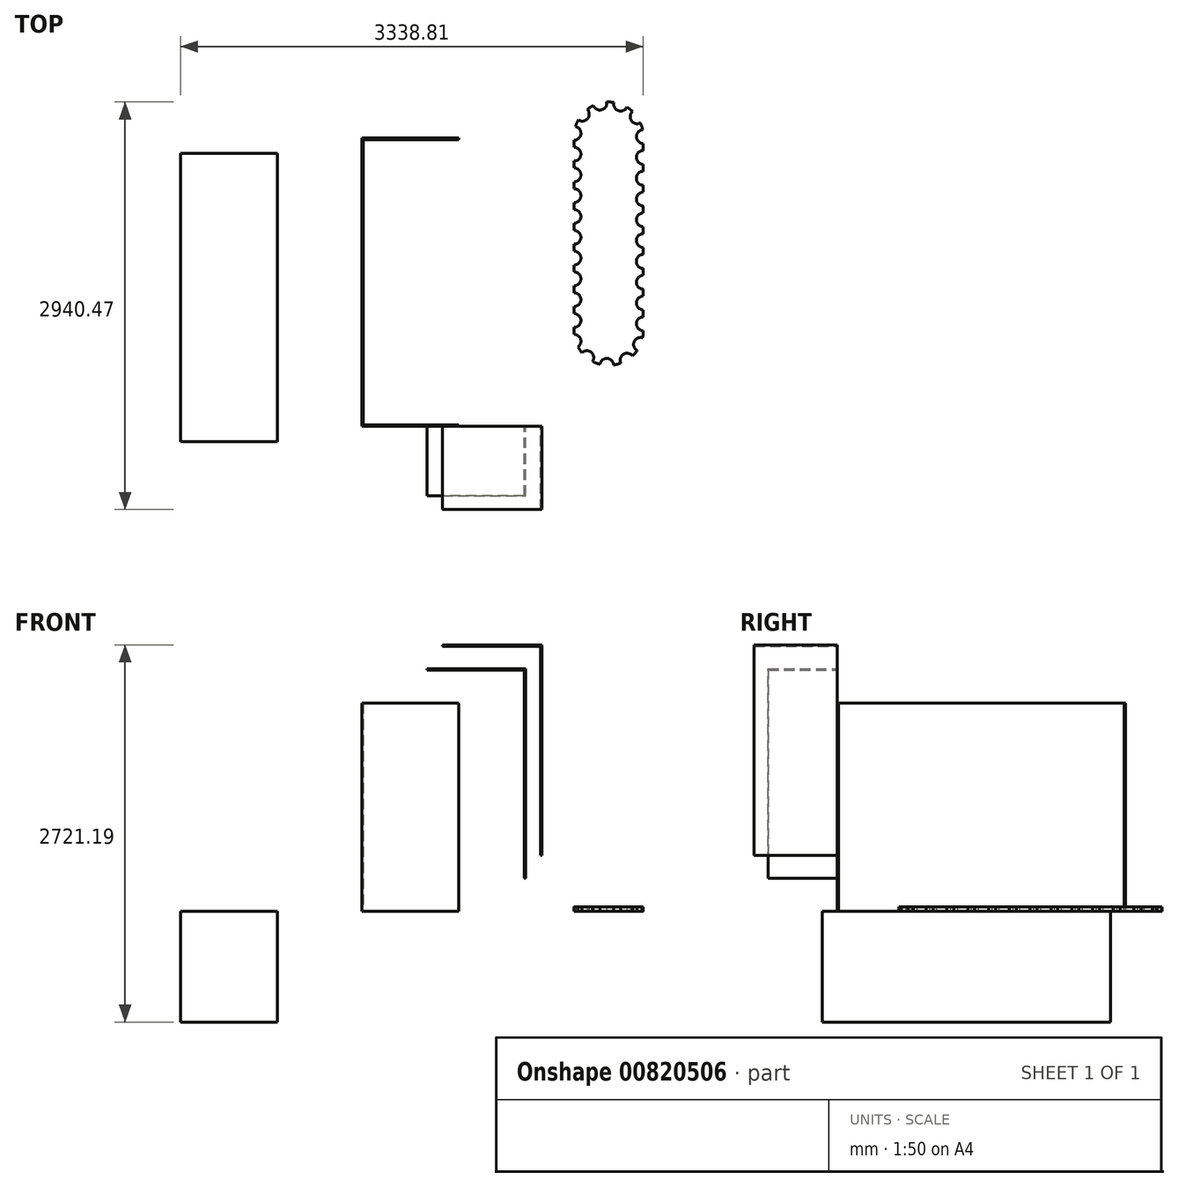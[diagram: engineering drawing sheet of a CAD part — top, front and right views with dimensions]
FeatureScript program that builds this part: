
annotation { "Feature Type Name" : "Feature", "Feature Type Description" : "" }
export const myFeature = defineFeature(function(context is Context, id is Id, definition is map)
    precondition{}
    {
        {
            var Q0;
            Q0=qCreatedBy(makeId("Top.planeOp"),FACE);
            var sketch = newSketch(context, id + "F0", { "sketchPlane" : qUnion([Q0])});
            skLineSegment(sketch, "E0", {"start": v(535.64, 2031.82) * mm, "end": v(535.64, -48.18) * mm});
            skLineSegment(sketch, "E1", {"start": v(535.64, -48.18) * mm, "end": v(-164.36, -48.18) * mm});
            skLineSegment(sketch, "E2", {"start": v(-164.36, -48.18) * mm, "end": v(-164.36, 2031.82) * mm});
            skLineSegment(sketch, "E3", {"start": v(-164.36, 2031.82) * mm, "end": v(535.64, 2031.82) * mm});
            skSolve(sketch);
        }
        {
            var Q0;
            Q0=makeQuery(id+"F0.imprint","IMPRINT",FACE,{"disambiguationData":[TD([[makeQuery(id+"F0.imprint","IMPRINT",EDGE,{"derivedFrom":sQuery(id+"F0.wireOp",EDGE,"E0")}),-1.0]])]});
            extrude(context, id + "F1", {"entities" : qUnion([Q0]), "depth" : 800 * mm, "offsetDistance" : 25 * mm});
        }
        {
            var Q0;
            Q0=makeQuery(id+"F1.opExtrude","CAP_FACE",FACE,{"disambiguationData":[OSD([sQuery(id+"F0.wireOp",EDGE,"E0"),sQuery(id+"F0.wireOp",EDGE,"E1"),sQuery(id+"F0.wireOp",EDGE,"E2"),sQuery(id+"F0.wireOp",EDGE,"E3")])],"isStart":false});
            var sketch = newSketch(context, id + "F2", { "sketchPlane" : qUnion([Q0])});
            skLineSegment(sketch, "E4", {"start": v(1843.77, 2140.47) * mm, "end": v(1143.77, 2140.47) * mm});
            skLineSegment(sketch, "E5", {"start": v(1143.77, 2140.47) * mm, "end": v(1143.77, 60.47) * mm});
            skLineSegment(sketch, "E6", {"start": v(1143.77, 60.47) * mm, "end": v(1843.77, 60.47) * mm});
            skLineSegment(sketch, "E7", {"start": v(1843.77, 60.47) * mm, "end": v(1843.77, 70.47) * mm});
            skLineSegment(sketch, "E8", {"start": v(1843.77, 70.47) * mm, "end": v(1153.77, 70.47) * mm});
            skLineSegment(sketch, "E9", {"start": v(1153.77, 70.47) * mm, "end": v(1153.77, 2130.47) * mm});
            skLineSegment(sketch, "E10", {"start": v(1153.77, 2130.47) * mm, "end": v(1843.77, 2130.47) * mm});
            skLineSegment(sketch, "E11", {"start": v(1843.77, 2130.47) * mm, "end": v(1843.77, 2140.47) * mm});
            skSolve(sketch);
        }
        {
            var Q0;
            Q0=makeQuery(id+"F2.imprint","IMPRINT",FACE,{"disambiguationData":[TD([[makeQuery(id+"F2.imprint","IMPRINT",EDGE,{"derivedFrom":sQuery(id+"F2.wireOp",EDGE,"E4")}),1.0]])]});
            extrude(context, id + "F3", {"entities" : qUnion([Q0]), "depth" : 1500 * mm, "offsetDistance" : 25 * mm});
        }
        {
            var Q0;
            Q0=makeQuery(id+"F3.opExtrude","SWEPT_FACE",FACE,{"disambiguationData":[OSD([sQuery(id+"F2.wireOp",EDGE,"E6")])]});
            var sketch = newSketch(context, id + "F4", { "sketchPlane" : qUnion([Q0])});
            skLineSegment(sketch, "E12", {"start": v(2314.75, 1037.76) * mm, "end": v(2314.75, 2537.76) * mm});
            skLineSegment(sketch, "E13", {"start": v(2314.75, 2537.76) * mm, "end": v(1614.75, 2537.76) * mm});
            skLineSegment(sketch, "E14", {"start": v(1614.75, 2537.76) * mm, "end": v(1614.75, 2547.76) * mm});
            skLineSegment(sketch, "E15", {"start": v(1614.75, 2547.76) * mm, "end": v(2324.75, 2547.76) * mm});
            skLineSegment(sketch, "E16", {"start": v(2324.75, 2547.76) * mm, "end": v(2324.75, 1037.76) * mm});
            skLineSegment(sketch, "E17", {"start": v(2324.75, 1037.76) * mm, "end": v(2314.75, 1037.76) * mm});
            skSolve(sketch);
        }
        {
            var Q0;
            Q0=makeQuery(id+"F4.imprint","IMPRINT",FACE,{"disambiguationData":[TD([[makeQuery(id+"F4.imprint","IMPRINT",EDGE,{"derivedFrom":sQuery(id+"F4.wireOp",EDGE,"E12")}),-1.0]])]});
            extrude(context, id + "F5", {"entities" : qUnion([Q0]), "depth" : 500 * mm, "offsetDistance" : 25 * mm});
        }
        {
            var Q0;
            Q0=makeQuery(id+"F3.opExtrude","SWEPT_FACE",FACE,{"disambiguationData":[OSD([sQuery(id+"F2.wireOp",EDGE,"E6")])]});
            var sketch = newSketch(context, id + "F6", { "sketchPlane" : qUnion([Q0])});
            skLineSegment(sketch, "E18", {"start": v(1724.02, 2711.19) * mm, "end": v(2434.02, 2711.19) * mm});
            skLineSegment(sketch, "E19", {"start": v(2434.02, 2711.19) * mm, "end": v(2434.02, 1201.19) * mm});
            skLineSegment(sketch, "E20", {"start": v(2434.02, 1201.19) * mm, "end": v(2444.02, 1201.19) * mm});
            skLineSegment(sketch, "E21", {"start": v(2444.02, 1201.19) * mm, "end": v(2444.02, 2721.19) * mm});
            skLineSegment(sketch, "E22", {"start": v(2444.02, 2721.19) * mm, "end": v(1724.02, 2721.19) * mm});
            skLineSegment(sketch, "E23", {"start": v(1724.02, 2721.19) * mm, "end": v(1724.02, 2711.19) * mm});
            skSolve(sketch);
        }
        {
            var Q0;
            Q0=makeQuery(id+"F6.imprint","IMPRINT",FACE,{"disambiguationData":[TD([[makeQuery(id+"F6.imprint","IMPRINT",EDGE,{"derivedFrom":sQuery(id+"F6.wireOp",EDGE,"E18")}),1.0]])]});
            extrude(context, id + "F7", {"entities" : qUnion([Q0]), "depth" : 600 * mm, "offsetDistance" : 25 * mm});
        }
        {
            var Q0;
            Q0=makeQuery(id+"F1.opExtrude","CAP_FACE",FACE,{"disambiguationData":[OSD([sQuery(id+"F0.wireOp",EDGE,"E0"),sQuery(id+"F0.wireOp",EDGE,"E1"),sQuery(id+"F0.wireOp",EDGE,"E2"),sQuery(id+"F0.wireOp",EDGE,"E3")])],"isStart":false});
            var sketch = newSketch(context, id + "F8", { "sketchPlane" : qUnion([Q0])});
            skLineSegment(sketch, "E24", {"start": v(3174.45, 2150.94) * mm, "end": v(3174.45, 750.94) * mm});
            skLineSegment(sketch, "E25", {"start": v(2674.45, 2150.94) * mm, "end": v(2674.45, 750.94) * mm});
            skArc(sketch, "E26", {"start": v(3174.45, 2150.94) * mm, "mid": v(2924.45, 2400.94) * mm, "end": v(2674.45, 2150.94) * mm});
            skArc(sketch, "E27", {"start": v(2674.45, 750.94) * mm, "mid": v(2924.45, 500.94) * mm, "end": v(3174.45, 750.94) * mm});
            skCircle(sketch, "E28", {"center": v(3174.45, 2150.94) * mm, "radius": 50 * mm});
            skCircle(sketch, "E29", {"center": v(3174.45, 2000.94) * mm, "radius": 50 * mm});
            skCircle(sketch, "E30", {"center": v(3174.45, 1850.94) * mm, "radius": 50 * mm});
            skCircle(sketch, "E31", {"center": v(3174.45, 1700.94) * mm, "radius": 50 * mm});
            skCircle(sketch, "E32", {"center": v(3174.45, 1550.94) * mm, "radius": 50 * mm});
            skCircle(sketch, "E33", {"center": v(3174.45, 1400.94) * mm, "radius": 50 * mm});
            skCircle(sketch, "E34", {"center": v(3174.45, 1250.94) * mm, "radius": 50 * mm});
            skCircle(sketch, "E35", {"center": v(3174.45, 1100.94) * mm, "radius": 50 * mm});
            skCircle(sketch, "E36", {"center": v(3174.45, 950.94) * mm, "radius": 50 * mm});
            skCircle(sketch, "E37", {"center": v(3174.45, 800.94) * mm, "radius": 50 * mm});
            skCircle(sketch, "E38", {"center": v(3154.17, 652.32) * mm, "radius": 50 * mm});
            skCircle(sketch, "E39", {"center": v(3129.45, 2294.03) * mm, "radius": 50 * mm});
            skCircle(sketch, "E40", {"center": v(3010.65, 2385.61) * mm, "radius": 50 * mm});
            skCircle(sketch, "E41", {"center": v(2860.82, 2392.71) * mm, "radius": 50 * mm});
            skCircle(sketch, "E42", {"center": v(2733.9, 2312.77) * mm, "radius": 50 * mm});
            skCircle(sketch, "E43", {"center": v(2674.45, 2175.05) * mm, "radius": 50 * mm});
            skCircle(sketch, "E44", {"center": v(2674.45, 2025.05) * mm, "radius": 50 * mm});
            skCircle(sketch, "E45", {"center": v(2674.45, 1875.05) * mm, "radius": 50 * mm});
            skCircle(sketch, "E46", {"center": v(2674.45, 1725.05) * mm, "radius": 50 * mm});
            skCircle(sketch, "E47", {"center": v(2674.45, 1575.05) * mm, "radius": 50 * mm});
            skCircle(sketch, "E48", {"center": v(2674.45, 1425.05) * mm, "radius": 50 * mm});
            skCircle(sketch, "E49", {"center": v(2674.45, 1275.05) * mm, "radius": 50 * mm});
            skCircle(sketch, "E50", {"center": v(2674.45, 1125.05) * mm, "radius": 50 * mm});
            skCircle(sketch, "E51", {"center": v(2674.45, 975.05) * mm, "radius": 50 * mm});
            skCircle(sketch, "E52", {"center": v(2674.45, 825.05) * mm, "radius": 50 * mm});
            skCircle(sketch, "E53", {"center": v(2674.45, 675.05) * mm, "radius": 50 * mm});
            skCircle(sketch, "E54", {"center": v(2766.84, 556.88) * mm, "radius": 50 * mm});
            skCircle(sketch, "E55", {"center": v(3056.37, 538.59) * mm, "radius": 50 * mm});
            skCircle(sketch, "E56", {"center": v(2911.08, 501.3) * mm, "radius": 50 * mm});
            skSolve(sketch);
        }
        {
            var Q0;
            {var subQ1=sQuery(id+"F8.wireOp",EDGE,"E24");var subQ7=sQuery(id+"F8.wireOp",EDGE,"E28");var subQ8=makeQuery(id+"F8.imprint","INTERSECT",VERTEX,{"derivedFrom":[subQ1,subQ7]});Q0=makeQuery(id+"F8.imprint","IMPRINT",FACE,{"disambiguationData":[TD([[makeQuery(id+"F8.imprint","IMPRINT",EDGE,{"disambiguationData":[TD([[subQ8,-1.0]])],"derivedFrom":subQ1}),-1.0]])]});}
            extrude(context, id + "F9", {"entities" : qUnion([Q0]), "depth" : 30 * mm, "offsetDistance" : 25 * mm});
        }
    });
